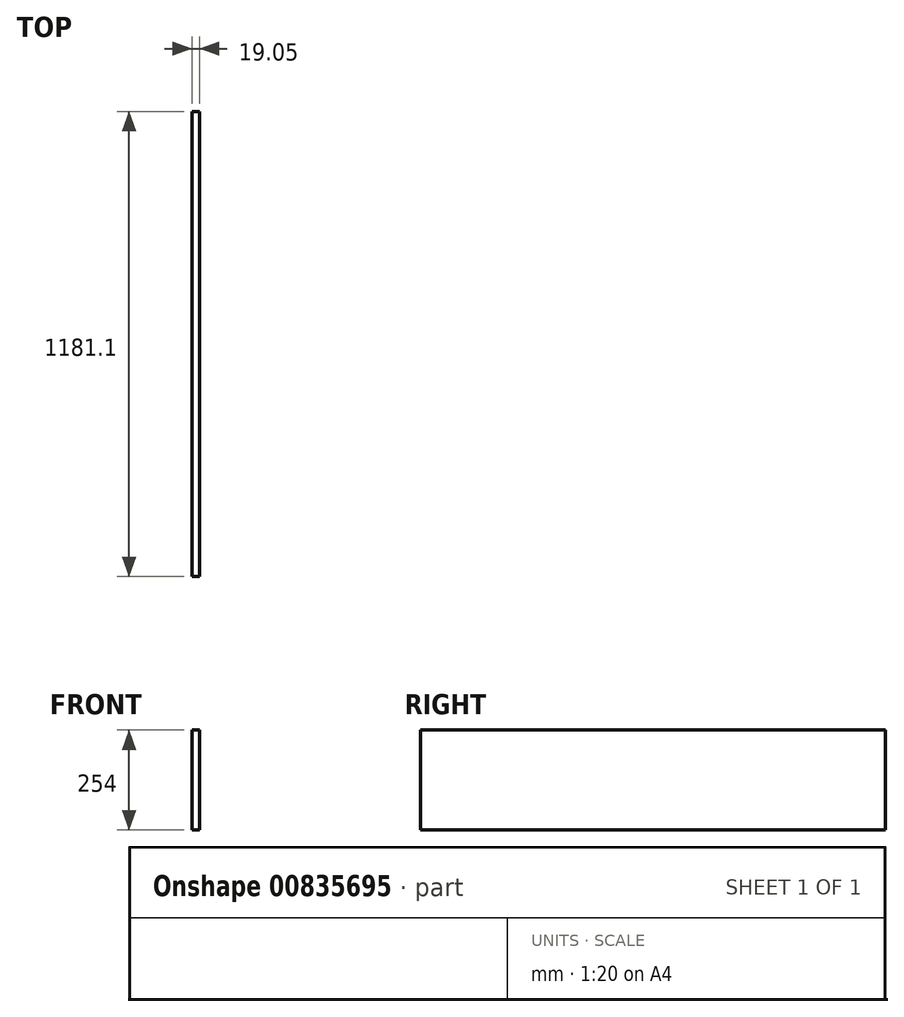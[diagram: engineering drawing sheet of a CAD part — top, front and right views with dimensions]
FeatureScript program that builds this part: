
annotation { "Feature Type Name" : "Feature", "Feature Type Description" : "" }
export const myFeature = defineFeature(function(context is Context, id is Id, definition is map)
    precondition{}
    {
        {
            var Q0;
            Q0=qCreatedBy(makeId("Right.planeOp"),FACE);
            var sketch = newSketch(context, id + "F0", { "sketchPlane" : qUnion([Q0])});
            skLineSegment(sketch, "E0.bottom", {"start": v(0, 0) * mm, "end": v(1181.1, 0) * mm});
            skLineSegment(sketch, "E0.top", {"start": v(0, 254) * mm, "end": v(1181.1, 254) * mm});
            skLineSegment(sketch, "E0.left", {"start": v(0, 0) * mm, "end": v(0, 254) * mm});
            skLineSegment(sketch, "E0.right", {"start": v(1181.1, 0) * mm, "end": v(1181.1, 254) * mm});
            skSolve(sketch);
        }
        {
            var Q0;
            Q0=qSketchRegion(id+"F0",true);
            extrude(context, id + "F1", {"entities" : qUnion([Q0]), "depth" : 19.05 * mm, "offsetDistance" : 25.4 * mm});
        }
    });
